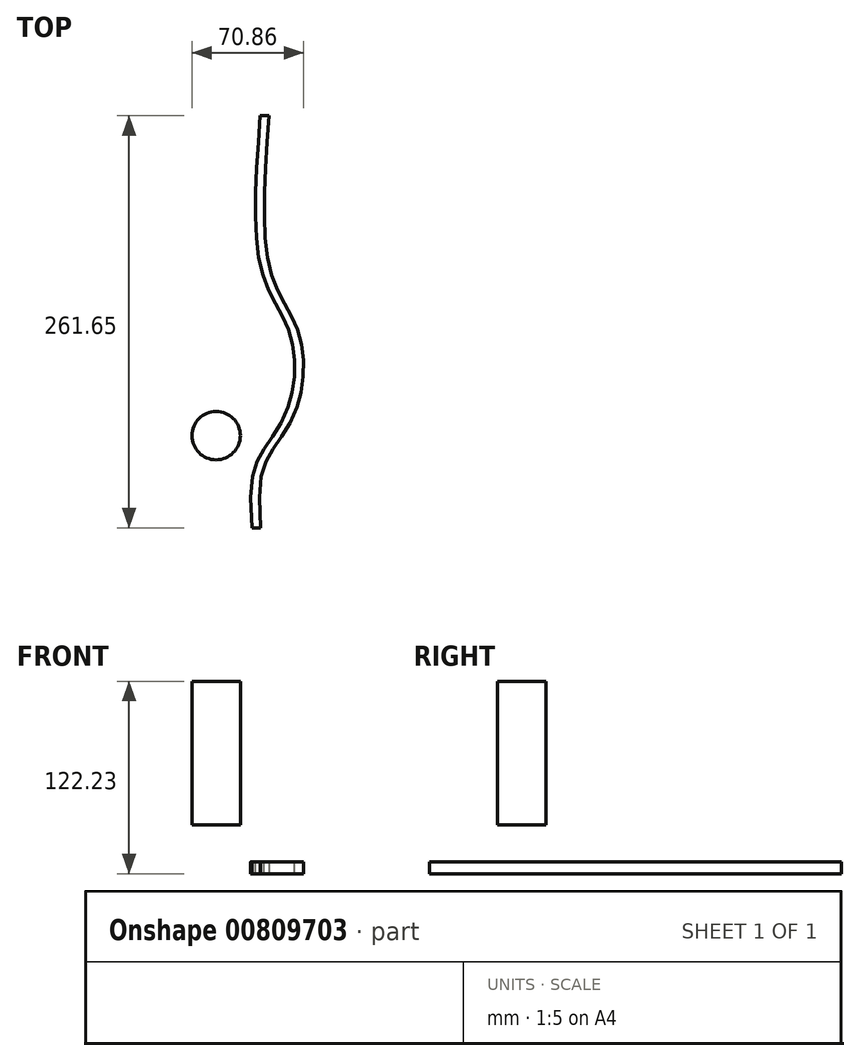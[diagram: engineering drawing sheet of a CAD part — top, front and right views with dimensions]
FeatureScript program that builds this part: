
annotation { "Feature Type Name" : "Feature", "Feature Type Description" : "" }
export const myFeature = defineFeature(function(context is Context, id is Id, definition is map)
    precondition{}
    {
        {
            var Q0;
            Q0=qCreatedBy(makeId("Top.planeOp"),FACE);
            var sketch = newSketch(context, id + "F0", { "sketchPlane" : qUnion([Q0])});
            skCircle(sketch, "E0", {"center": v(-34.67, -16.59) * mm, "radius": 15.37 * mm});
            skSolve(sketch);
        }
        {
            var Q0;
            Q0 = qSketchRegion(id + "F0", true);
            extrude(context, id + "F1", {"entities" : qUnion([Q0]), "depth" : 91.19 * mm, "offsetDistance" : 25.4 * mm});
        }
        {
            var Q0;
            Q0=qCreatedBy(makeId("Top.planeOp"),FACE);
            var sketch = newSketch(context, id + "F2", { "sketchPlane" : qUnion([Q0])});
            skFitSpline(sketch, "E1", {"points": [v(27.43, -75.1) * mm, v(34.18, -26.67) * mm, v(49.95, 0) * mm, v(52.1, 46.48) * mm, v(34.11, 86.37) * mm, v(32.74, 186.56) * mm], "startDerivative": vector(-40.4, 443.89) * mm, "endDerivative": vector(29.73, 421.24) * mm});
            skSolve(sketch);
        }
        {
            var Q0;
            Q0=qCreatedBy(makeId("Front.planeOp"),FACE);
            var sketch = newSketch(context, id + "F3", { "sketchPlane" : qUnion([Q0])});
            skLineSegment(sketch, "E2.bottom", {"start": v(10.5, -23.66) * mm, "end": v(16.16, -23.66) * mm});
            skLineSegment(sketch, "E2.top", {"start": v(10.5, -31.04) * mm, "end": v(16.16, -31.04) * mm});
            skLineSegment(sketch, "E2.left", {"start": v(10.5, -23.66) * mm, "end": v(10.5, -31.04) * mm});
            skLineSegment(sketch, "E2.right", {"start": v(16.16, -23.66) * mm, "end": v(16.16, -31.04) * mm});
            skSolve(sketch);
        }
        {
            var Q0;
            Q0=makeQuery(id+"F3.imprint","IMPRINT",FACE,{"disambiguationData":[TD([[makeQuery(id+"F3.imprint","IMPRINT",EDGE,{"derivedFrom":sQuery(id+"F3.wireOp",EDGE,"E2.bottom")}),-1.0]])]});
            var Q1;
            Q1=sQuery(id+"F2.wireOp",EDGE,"E1");
            sweep(context, id + "F4", {"profiles" : qUnion([Q0]), "path" : qUnion([Q1]), "keepProfileOrientation" : true});
        }
    });
